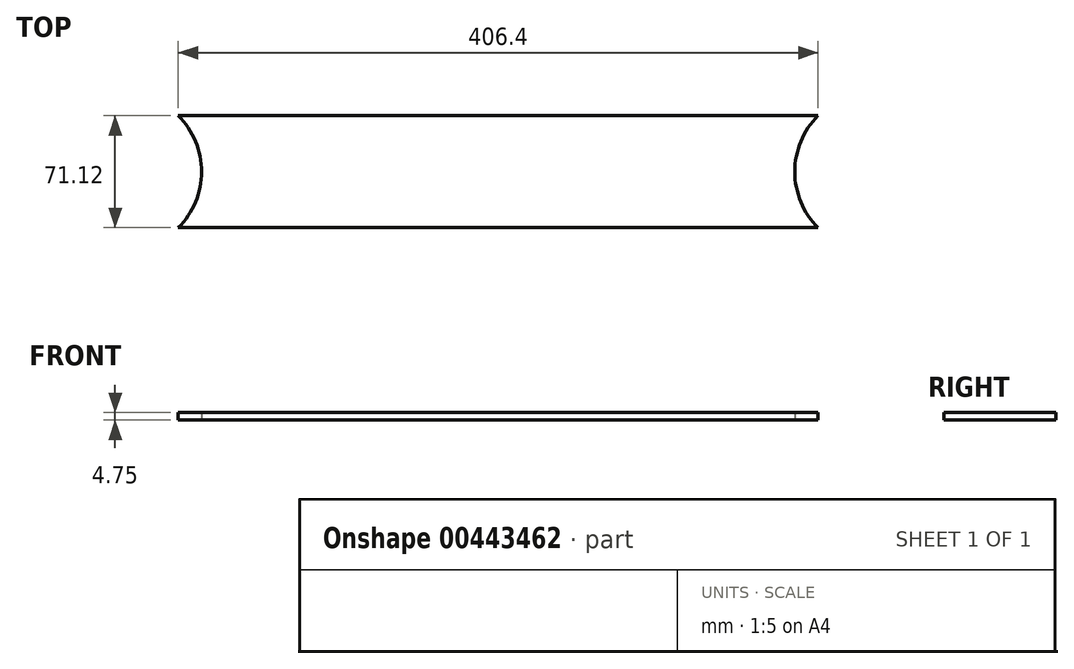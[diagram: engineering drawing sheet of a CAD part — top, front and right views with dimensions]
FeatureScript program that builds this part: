
annotation { "Feature Type Name" : "Feature", "Feature Type Description" : "" }
export const myFeature = defineFeature(function(context is Context, id is Id, definition is map)
    precondition{}
    {
        {
            var Q0;
            Q0=qCreatedBy(makeId("Top.planeOp"),FACE);
            var sketch = newSketch(context, id + "F0", { "sketchPlane" : qUnion([Q0])});
            skLineSegment(sketch, "E0.bottom", {"start": v(-190.8, 39.3) * mm, "end": v(215.6, 39.3) * mm});
            skLineSegment(sketch, "E0.top", {"start": v(-190.8, -31.82) * mm, "end": v(215.6, -31.82) * mm});
            skArc(sketch, "E1", {"start": v(-190.8, -31.82) * mm, "mid": v(-175.9, 3.74) * mm, "end": v(-190.8, 39.3) * mm});
            skArc(sketch, "E2", {"start": v(215.6, 39.3) * mm, "mid": v(200.81, 3.74) * mm, "end": v(215.6, -31.82) * mm});
            skSolve(sketch);
        }
        {
            var Q0;
            Q0=makeQuery(id+"F0.imprint","IMPRINT",FACE,{"disambiguationData":[TD([[makeQuery(id+"F0.imprint","IMPRINT",EDGE,{"derivedFrom":sQuery(id+"F0.wireOp",EDGE,"E0.bottom")}),-1.0]])]});
            extrude(context, id + "F1", {"entities" : qUnion([Q0]), "depth" : 4.75 * mm});
        }
    });
